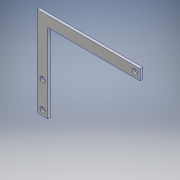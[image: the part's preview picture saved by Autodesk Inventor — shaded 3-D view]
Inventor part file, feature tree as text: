
AUTODESK INVENTOR PART (.ipt)
format: ipt  version: 2018.1 (Build 221171000, 171)  size: 113,152 bytes
history: native  units: mm
features: extrude x1, sketch x1
ambient origin geometry x8: Origin, YZ Plane, XZ Plane, XY Plane, X Axis, Y Axis, Z Axis, Center Point
bodies: Body1 (feature_tree)
feature tree (2):
  extrude  "押し出し4"  Depth=195.0mm
  sketch  "スケッチ1"
